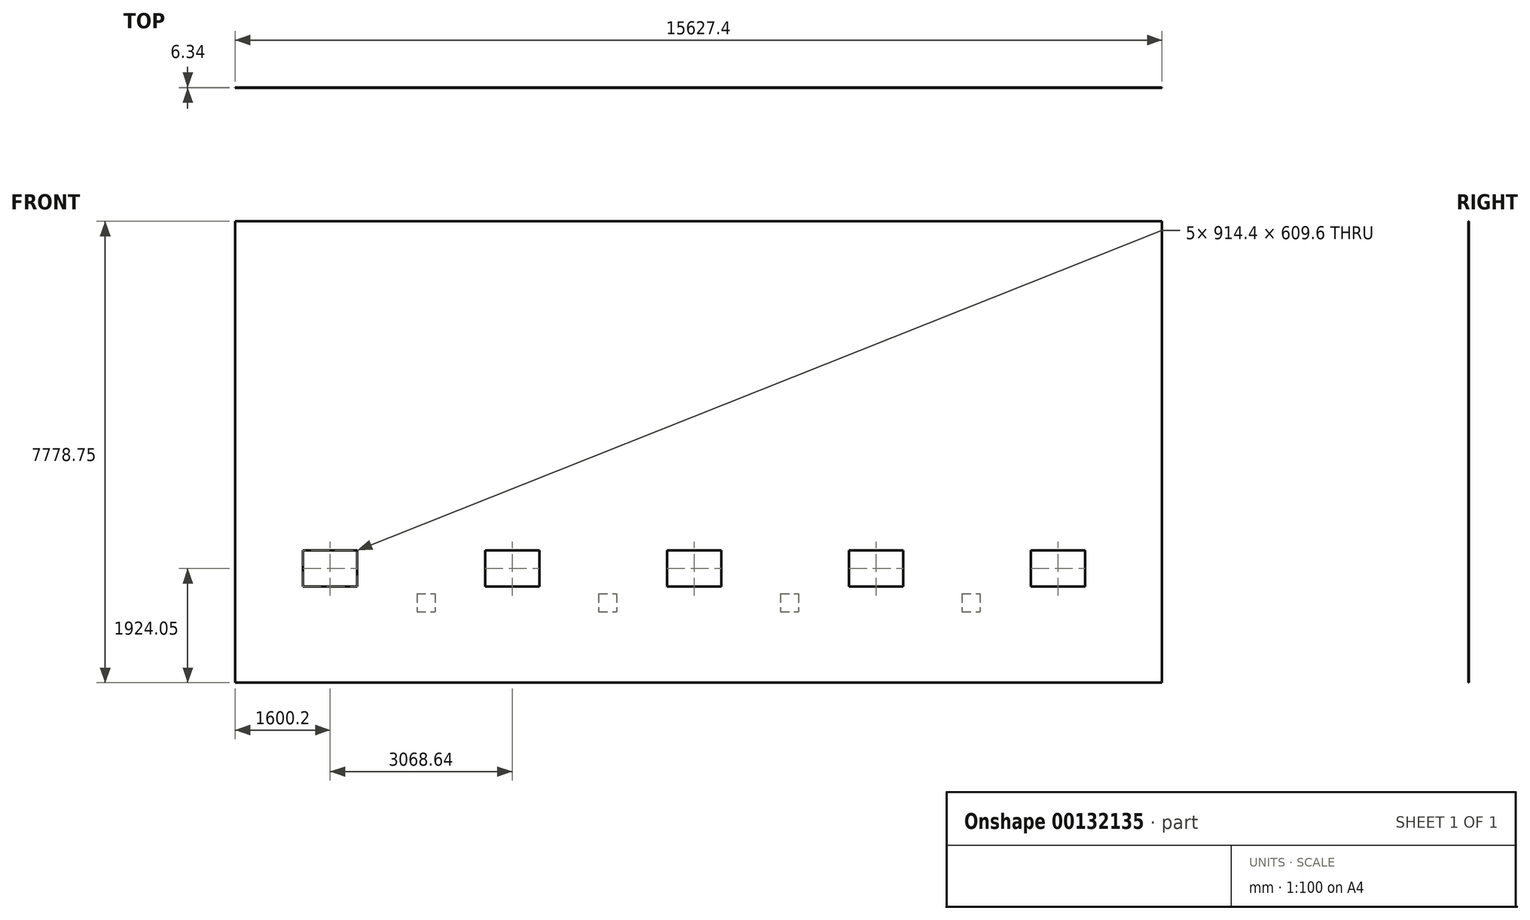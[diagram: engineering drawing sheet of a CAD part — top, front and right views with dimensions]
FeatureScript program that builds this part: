
annotation { "Feature Type Name" : "Feature", "Feature Type Description" : "" }
export const myFeature = defineFeature(function(context is Context, id is Id, definition is map)
    precondition{}
    {
        {
            var Q0;
            Q0=qCreatedBy(makeId("Front.planeOp"),FACE);
            var sketch = newSketch(context, id + "F0", { "sketchPlane" : qUnion([Q0])});
            skLineSegment(sketch, "E0.bottom", {"start": v(0, 0) * mm, "end": v(15627.35, 0) * mm});
            skLineSegment(sketch, "E0.top", {"start": v(0, 7778.75) * mm, "end": v(15627.35, 7778.75) * mm});
            skLineSegment(sketch, "E0.left", {"start": v(0, 0) * mm, "end": v(0, 7778.75) * mm});
            skLineSegment(sketch, "E0.right", {"start": v(15627.35, 0) * mm, "end": v(15627.35, 7778.75) * mm});
            skSolve(sketch);
        }
        {
            var Q0;
            Q0 = qSketchRegion(id + "F0", true);
            extrude(context, id + "F1", {"entities" : qUnion([Q0]), "depth" : 3.17 * mm});
        }
        {
            var Q0;
            Q0=makeQuery(id+"F1.opExtrude","CAP_FACE",FACE,{"disambiguationData":[OSD([sQuery(id+"F0.wireOp",EDGE,"E0.bottom"),sQuery(id+"F0.wireOp",EDGE,"E0.top"),sQuery(id+"F0.wireOp",EDGE,"E0.left"),sQuery(id+"F0.wireOp",EDGE,"E0.right")])],"isStart":false});
            var sketch = newSketch(context, id + "F2", { "sketchPlane" : qUnion([Q0])});
            skLineSegment(sketch, "E1", {"start": v(0, 254) * mm, "end": v(15627.35, 254) * mm});
            skLineSegment(sketch, "E2", {"start": v(15627.35, 7600.95) * mm, "end": v(0, 7600.95) * mm});
            skLineSegment(sketch, "E3", {"start": v(0, 2889.25) * mm, "end": v(15627.35, 2889.25) * mm});
            skPoint(sketch, "E3.endSnap0", {"position": v(15627.35, 3889.38) * mm});
            skSolve(sketch);
        }
        {
            var Q0;
            Q0=makeQuery(id+"F1.opExtrude","CAP_FACE",FACE,{"disambiguationData":[OSD([sQuery(id+"F0.wireOp",EDGE,"E0.bottom"),sQuery(id+"F0.wireOp",EDGE,"E0.top"),sQuery(id+"F0.wireOp",EDGE,"E0.left"),sQuery(id+"F0.wireOp",EDGE,"E0.right")])],"isStart":false});
            var sketch = newSketch(context, id + "F3", { "sketchPlane" : qUnion([Q0])});
            skLineSegment(sketch, "E4.bottom", {"start": v(3063.88, 1498.6) * mm, "end": v(3368.68, 1498.6) * mm});
            skLineSegment(sketch, "E4.top", {"start": v(3063.88, 1193.8) * mm, "end": v(3368.68, 1193.8) * mm});
            skLineSegment(sketch, "E4.left", {"start": v(3063.88, 1498.6) * mm, "end": v(3063.88, 1193.8) * mm});
            skLineSegment(sketch, "E4.right", {"start": v(3368.68, 1498.6) * mm, "end": v(3368.68, 1193.8) * mm});
            skLineSegment(sketch, "E5.bottom", {"start": v(6127.75, 1498.6) * mm, "end": v(6432.55, 1498.6) * mm});
            skLineSegment(sketch, "E5.top", {"start": v(6127.75, 1193.8) * mm, "end": v(6432.55, 1193.8) * mm});
            skLineSegment(sketch, "E5.left", {"start": v(6127.75, 1498.6) * mm, "end": v(6127.75, 1193.8) * mm});
            skLineSegment(sketch, "E5.right", {"start": v(6432.55, 1498.6) * mm, "end": v(6432.55, 1193.8) * mm});
            skPoint(sketch, "E6.firstSnap0", {"position": v(6280.15, 1498.6) * mm});
            skLineSegment(sketch, "E6.bottom", {"start": v(9191.63, 1498.6) * mm, "end": v(9496.43, 1498.6) * mm});
            skLineSegment(sketch, "E6.top", {"start": v(9191.63, 1193.8) * mm, "end": v(9496.43, 1193.8) * mm});
            skLineSegment(sketch, "E6.left", {"start": v(9191.63, 1498.6) * mm, "end": v(9191.63, 1193.8) * mm});
            skLineSegment(sketch, "E6.right", {"start": v(9496.43, 1498.6) * mm, "end": v(9496.43, 1193.8) * mm});
            skPoint(sketch, "E7.oppositeSnap0", {"position": v(9344.03, 1193.8) * mm});
            skLineSegment(sketch, "E7.bottom", {"start": v(12255.5, 1498.6) * mm, "end": v(12560.3, 1498.6) * mm});
            skLineSegment(sketch, "E7.top", {"start": v(12255.5, 1193.8) * mm, "end": v(12560.3, 1193.8) * mm});
            skLineSegment(sketch, "E7.left", {"start": v(12255.5, 1498.6) * mm, "end": v(12255.5, 1193.8) * mm});
            skLineSegment(sketch, "E7.right", {"start": v(12560.3, 1498.6) * mm, "end": v(12560.3, 1193.8) * mm});
            skSolve(sketch);
        }
        {
            var Q0;
            {var subQ0=sQuery(id+"F2.wireOp",EDGE,"E1");Q0=makeQuery(id+"F2.imprint","IMPRINT",FACE,{"disambiguationData":[TD([[makeQuery(id+"F2.imprint","IMPRINT",EDGE,{"derivedFrom":subQ0}),1.0]])]});}
            var sketch = newSketch(context, id + "F4", { "sketchPlane" : qUnion([Q0])});
            skLineSegment(sketch, "E8.bottom", {"start": v(1143, 2228.85) * mm, "end": v(2057.4, 2228.85) * mm});
            skLineSegment(sketch, "E8.top", {"start": v(1143, 1619.25) * mm, "end": v(2057.4, 1619.25) * mm});
            skLineSegment(sketch, "E8.left", {"start": v(1143, 2228.85) * mm, "end": v(1143, 1619.25) * mm});
            skLineSegment(sketch, "E8.right", {"start": v(2057.4, 2228.85) * mm, "end": v(2057.4, 1619.25) * mm});
            skPoint(sketch, "E9.firstSnap0", {"position": v(1600.2, 2228.85) * mm});
            skPoint(sketch, "E9.oppositeSnap0", {"position": v(1600.2, 1619.25) * mm});
            skLineSegment(sketch, "E9.bottom", {"start": v(4211.64, 2228.85) * mm, "end": v(5126.04, 2228.85) * mm});
            skLineSegment(sketch, "E9.top", {"start": v(4211.64, 1619.25) * mm, "end": v(5126.04, 1619.25) * mm});
            skLineSegment(sketch, "E9.left", {"start": v(4211.64, 2228.85) * mm, "end": v(4211.64, 1619.25) * mm});
            skLineSegment(sketch, "E9.right", {"start": v(5126.04, 2228.85) * mm, "end": v(5126.04, 1619.25) * mm});
            skLineSegment(sketch, "E10.bottom", {"start": v(7280.27, 2228.85) * mm, "end": v(8194.67, 2228.85) * mm});
            skLineSegment(sketch, "E10.top", {"start": v(7280.27, 1619.25) * mm, "end": v(8194.67, 1619.25) * mm});
            skLineSegment(sketch, "E10.left", {"start": v(7280.27, 2228.85) * mm, "end": v(7280.27, 1619.25) * mm});
            skLineSegment(sketch, "E10.right", {"start": v(8194.67, 2228.85) * mm, "end": v(8194.67, 1619.25) * mm});
            skPoint(sketch, "E11.firstSnap0", {"position": v(7737.47, 2228.85) * mm});
            skLineSegment(sketch, "E11.bottom", {"start": v(10348.91, 2228.85) * mm, "end": v(11263.31, 2228.85) * mm});
            skLineSegment(sketch, "E11.top", {"start": v(10348.91, 1619.25) * mm, "end": v(11263.31, 1619.25) * mm});
            skLineSegment(sketch, "E11.left", {"start": v(10348.91, 2228.85) * mm, "end": v(10348.91, 1619.25) * mm});
            skLineSegment(sketch, "E11.right", {"start": v(11263.31, 2228.85) * mm, "end": v(11263.31, 1619.25) * mm});
            skLineSegment(sketch, "E12.bottom", {"start": v(13417.55, 2228.85) * mm, "end": v(14331.95, 2228.85) * mm});
            skLineSegment(sketch, "E12.top", {"start": v(13417.55, 1619.25) * mm, "end": v(14331.95, 1619.25) * mm});
            skLineSegment(sketch, "E12.left", {"start": v(13417.55, 2228.85) * mm, "end": v(13417.55, 1619.25) * mm});
            skLineSegment(sketch, "E12.right", {"start": v(14331.95, 2228.85) * mm, "end": v(14331.95, 1619.25) * mm});
            skSolve(sketch);
        }
        {
            var Q0;
            Q0 = qSketchRegion(id + "F4", true);
            extrude(context, id + "F5", {"entities" : qUnion([Q0]), "operationType" : NewBodyOperationType.REMOVE, "endBound" : BoundingType.UP_TO_NEXT, "oppositeDirection" : true, "depth" : 25.4 * mm});
        }
        {
            var Q0;
            Q0 = qSketchRegion(id + "F3", true);
            extrude(context, id + "F6", {"entities" : qUnion([Q0]), "operationType" : NewBodyOperationType.ADD, "oppositeDirection" : true, "depth" : 6.35 * mm});
        }
    });
